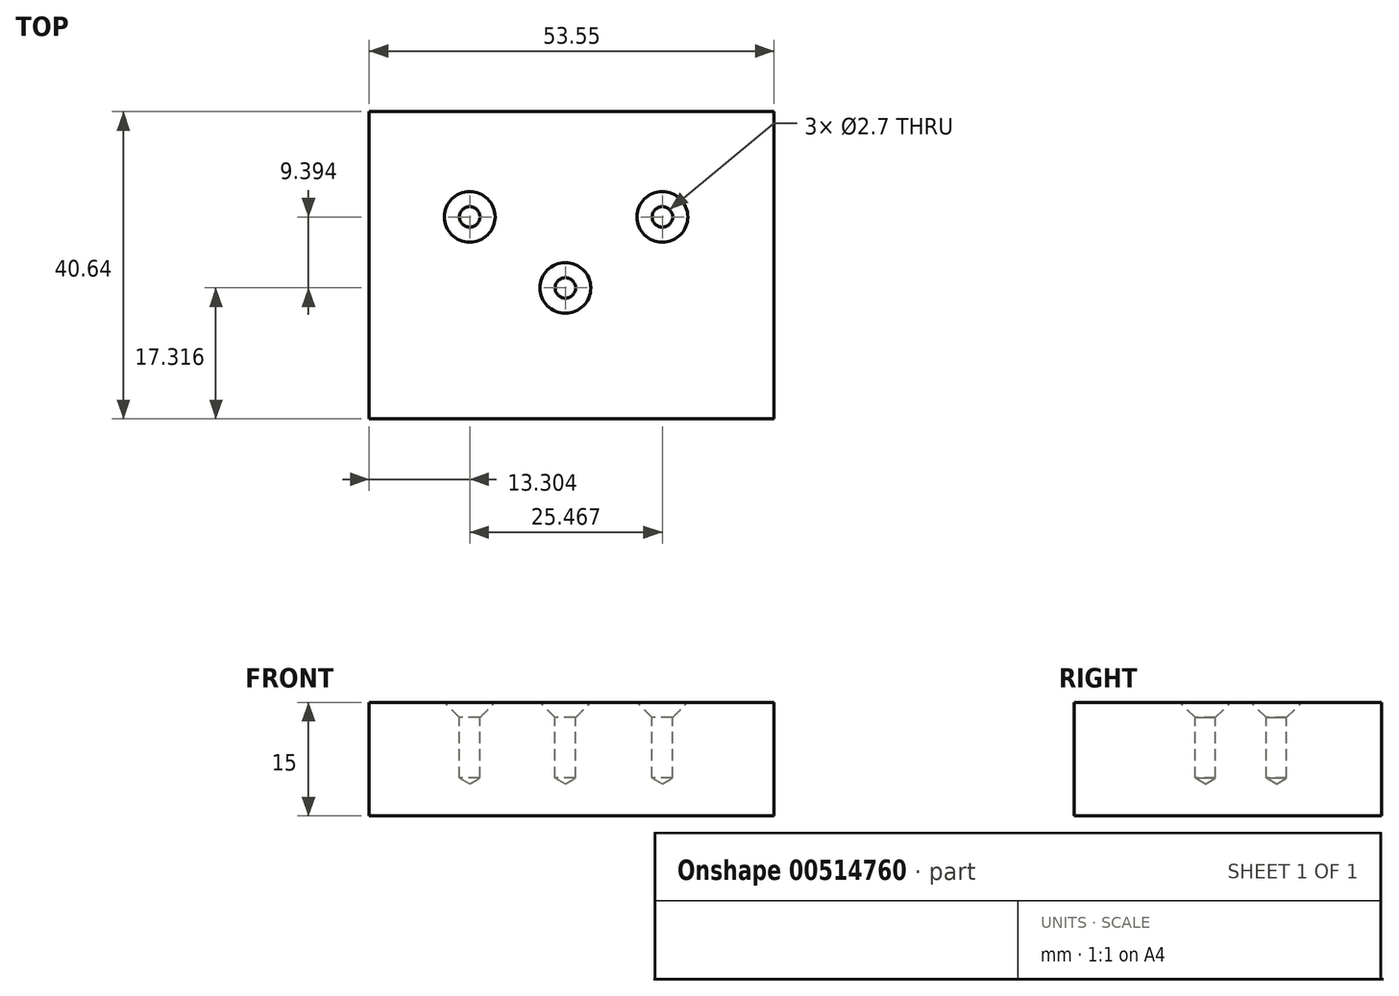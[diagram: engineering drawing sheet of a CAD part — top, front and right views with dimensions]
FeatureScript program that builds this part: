
annotation { "Feature Type Name" : "Feature", "Feature Type Description" : "" }
export const myFeature = defineFeature(function(context is Context, id is Id, definition is map)
    precondition{}
    {
        {
            var Q0;
            Q0=qCreatedBy(makeId("Top.planeOp"),FACE);
            var sketch = newSketch(context, id + "F0", { "sketchPlane" : qUnion([Q0])});
            skLineSegment(sketch, "E0.bottom", {"start": v(-20.24, 13.93) * mm, "end": v(33.3, 13.93) * mm});
            skLineSegment(sketch, "E0.top", {"start": v(-20.24, -26.7) * mm, "end": v(33.3, -26.7) * mm});
            skLineSegment(sketch, "E0.left", {"start": v(-20.24, 13.93) * mm, "end": v(-20.24, -26.7) * mm});
            skLineSegment(sketch, "E0.right", {"start": v(33.3, 13.93) * mm, "end": v(33.3, -26.7) * mm});
            skSolve(sketch);
        }
        {
            var Q0;
            Q0 = qSketchRegion(id + "F0", true);
            extrude(context, id + "F1", {"entities" : qUnion([Q0]), "depth" : 15 * mm, "offsetDistance" : 25 * mm});
        }
        {
            var Q0;
            Q0=makeQuery(id+"F1.opExtrude","CAP_FACE",FACE,{"disambiguationData":[OSD([sQuery(id+"F0.wireOp",EDGE,"E0.bottom"),sQuery(id+"F0.wireOp",EDGE,"E0.top"),sQuery(id+"F0.wireOp",EDGE,"E0.left"),sQuery(id+"F0.wireOp",EDGE,"E0.right")])],"isStart":false});
            var sketch = newSketch(context, id + "F2", { "sketchPlane" : qUnion([Q0])});
            skPoint(sketch, "E1", {"position": v(-6.94, 0) * mm});
            skPoint(sketch, "E2", {"position": v(18.53, 0) * mm});
            skPoint(sketch, "E3", {"position": v(5.7, -9.4) * mm});
            skSolve(sketch);
        }
        {
            var Q0;
            Q0=sQuery(id+"F2.wireOp",VERTEX,"E1");
            var Q1;
            Q1=sQuery(id+"F2.wireOp",VERTEX,"E3");
            var Q2;
            Q2=sQuery(id+"F2.wireOp",VERTEX,"E2");
            var Q3;
            Q3=makeQuery(id+"F1.opExtrude","SWEPT_BODY",BODY,{"disambiguationData":[OSD([sQuery(id+"F0.wireOp",EDGE,"E0.bottom"),sQuery(id+"F0.wireOp",EDGE,"E0.top"),sQuery(id+"F0.wireOp",EDGE,"E0.left"),sQuery(id+"F0.wireOp",EDGE,"E0.right")])]});
            hole(context, id + "F3", {"style" : HoleStyle.C_SINK, "endStyle" : HoleEndStyle.BLIND, "standardTappedOrClearance" : lookupTablePath({ "standard" : "ISO", "engagement" : "50%", "pitch" : "0.5 mm", "size" : "M3", "type" : "Tapped" }), "standardBlindInLast" : lookupTablePath({ "standard" : "ISO", "engagement" : "50%", "pitch" : "0.5 mm", "size" : "M3", "type" : "Tapped" }), "holeDiameter" : 2.7 * mm, "cSinkDiameter" : 6.72 * mm, "cSinkAngle" : 90 * degree, "showTappedDepth" : true, "holeDepth" : 10 * mm, "isTappedThrough" : true, "tappedDepth" : 8 * mm, "tapClearance" : 4, "locations" : qUnion([Q0, Q1, Q2]), "scope" : qUnion([Q3]), "majorDiameter" : 3 * mm});
        }
    });
